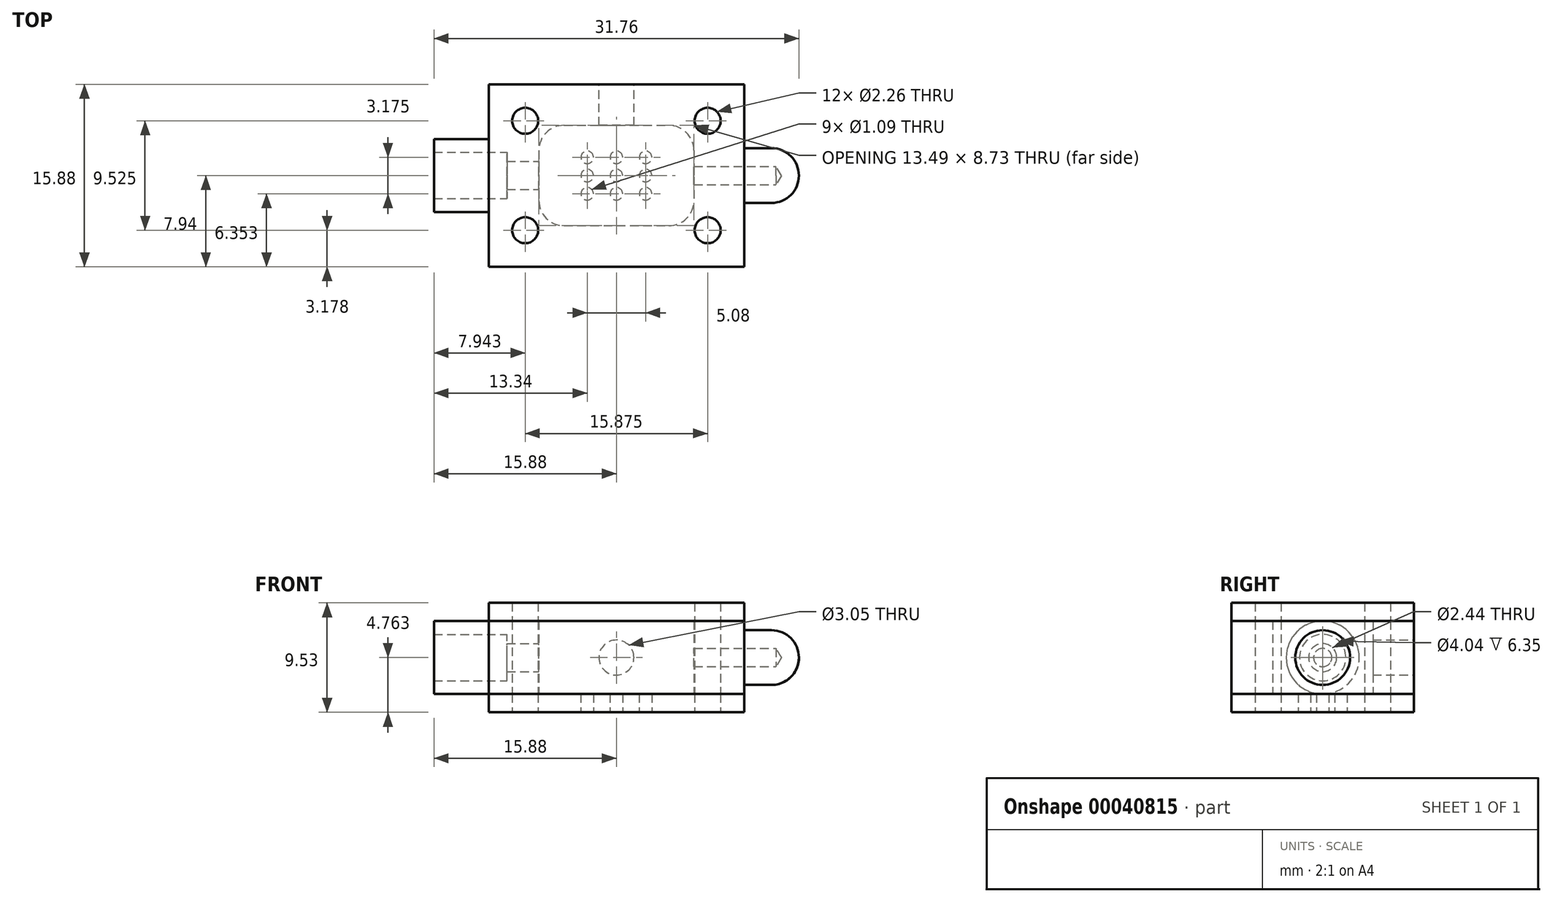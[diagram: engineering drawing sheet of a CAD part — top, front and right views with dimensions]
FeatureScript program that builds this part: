
annotation { "Feature Type Name" : "Feature", "Feature Type Description" : "" }
export const myFeature = defineFeature(function(context is Context, id is Id, definition is map)
    precondition{}
    {
        {
            var Q0;
            Q0=qCreatedBy(makeId("Top.planeOp"),FACE);
            var sketch = newSketch(context, id + "F0", { "sketchPlane" : qUnion([Q0])});
            skLineSegment(sketch, "E0.rect.bottom", {"start": v(-11.11, 7.94) * mm, "end": v(11.11, 7.94) * mm});
            skLineSegment(sketch, "E0.rect.top", {"start": v(-11.11, -7.94) * mm, "end": v(11.11, -7.94) * mm});
            skLineSegment(sketch, "E0.rect.left", {"start": v(-11.11, 7.94) * mm, "end": v(-11.11, -7.94) * mm});
            skLineSegment(sketch, "E0.rect.right", {"start": v(11.11, 7.94) * mm, "end": v(11.11, -7.94) * mm});
            skPoint(sketch, "E0.rect.middle", {"position": v(0, 0) * mm});
            skLineSegment(sketch, "E1.rect.bottom", {"start": v(-4.56, 4.37) * mm, "end": v(4.56, 4.37) * mm});
            skLineSegment(sketch, "E1.rect.top", {"start": v(-4.56, -4.37) * mm, "end": v(4.56, -4.37) * mm});
            skLineSegment(sketch, "E1.rect.left", {"start": v(-6.75, 2.18) * mm, "end": v(-6.75, -2.18) * mm});
            skLineSegment(sketch, "E1.rect.right", {"start": v(6.75, 2.18) * mm, "end": v(6.75, -2.18) * mm});
            skPoint(sketch, "E2.visualSharp", {"position": v(-6.75, 4.37) * mm});
            skArc(sketch, "E2.filletArc", {"start": v(-4.56, 4.37) * mm, "mid": v(-6.1, 3.73) * mm, "end": v(-6.75, 2.18) * mm});
            skPoint(sketch, "E3.visualSharp", {"position": v(-6.75, -4.37) * mm});
            skArc(sketch, "E3.filletArc", {"start": v(-6.75, -2.18) * mm, "mid": v(-6.1, -3.73) * mm, "end": v(-4.56, -4.37) * mm});
            skPoint(sketch, "E4.visualSharp", {"position": v(6.75, -4.37) * mm});
            skArc(sketch, "E4.filletArc", {"start": v(4.56, -4.37) * mm, "mid": v(6.1, -3.73) * mm, "end": v(6.75, -2.18) * mm});
            skPoint(sketch, "E5.visualSharp", {"position": v(6.75, 4.37) * mm});
            skArc(sketch, "E5.filletArc", {"start": v(6.75, 2.18) * mm, "mid": v(6.1, 3.73) * mm, "end": v(4.56, 4.37) * mm});
            skSolve(sketch);
        }
        {
            var Q0;
            Q0=makeQuery(id+"F0.imprint","IMPRINT",FACE,{"disambiguationData":[TD([[makeQuery(id+"F0.imprint","IMPRINT",EDGE,{"derivedFrom":sQuery(id+"F0.wireOp",EDGE,"E0.rect.bottom")}),-1.0]])]});
            extrude(context, id + "F1", {"entities" : qUnion([Q0]), "depth" : 6.35 * mm});
        }
        {
            var Q0;
            Q0=makeQuery(id+"F1.opExtrude","CAP_FACE",FACE,{"disambiguationData":[OSD([sQuery(id+"F0.wireOp",EDGE,"E0.rect.bottom"),sQuery(id+"F0.wireOp",EDGE,"E0.rect.top"),sQuery(id+"F0.wireOp",EDGE,"E0.rect.left"),sQuery(id+"F0.wireOp",EDGE,"E0.rect.right"),sQuery(id+"F0.wireOp",EDGE,"E1.rect.bottom"),sQuery(id+"F0.wireOp",EDGE,"E1.rect.top"),sQuery(id+"F0.wireOp",EDGE,"E1.rect.left"),sQuery(id+"F0.wireOp",EDGE,"E1.rect.right"),sQuery(id+"F0.wireOp",EDGE,"E2.filletArc"),sQuery(id+"F0.wireOp",EDGE,"E3.filletArc"),sQuery(id+"F0.wireOp",EDGE,"E4.filletArc"),sQuery(id+"F0.wireOp",EDGE,"E5.filletArc")])],"isStart":false});
            var sketch = newSketch(context, id + "F2", { "sketchPlane" : qUnion([Q0])});
            skLineSegment(sketch, "E6", {"start": v(-7.94, 10.98) * mm, "end": v(-7.94, -12.77) * mm, "construction": true});
            skLineSegment(sketch, "E7", {"start": v(7.94, 10.98) * mm, "end": v(7.94, -12.77) * mm, "construction": true});
            skLineSegment(sketch, "E8", {"start": v(13.6, 4.76) * mm, "end": v(-15.56, 4.76) * mm, "construction": true});
            skLineSegment(sketch, "E9", {"start": v(13.6, -4.76) * mm, "end": v(-15.56, -4.76) * mm, "construction": true});
            skPoint(sketch, "E10", {"position": v(-7.94, 4.76) * mm});
            skPoint(sketch, "E11", {"position": v(7.94, 4.76) * mm});
            skPoint(sketch, "E12", {"position": v(7.94, -4.76) * mm});
            skPoint(sketch, "E13", {"position": v(-7.94, -4.76) * mm});
            skSolve(sketch);
        }
        {
            var Q0;
            Q0=sQuery(id+"F2.wireOp",VERTEX,"E10");
            var Q1;
            Q1=sQuery(id+"F2.wireOp",VERTEX,"E11");
            var Q2;
            Q2=sQuery(id+"F2.wireOp",VERTEX,"E12");
            var Q3;
            Q3=sQuery(id+"F2.wireOp",VERTEX,"E13");
            var Q4;
            Q4=makeQuery(id+"F1.opExtrude","SWEPT_BODY",BODY,{"disambiguationData":[OSD([sQuery(id+"F0.wireOp",EDGE,"E0.rect.bottom"),sQuery(id+"F0.wireOp",EDGE,"E0.rect.top"),sQuery(id+"F0.wireOp",EDGE,"E0.rect.left"),sQuery(id+"F0.wireOp",EDGE,"E0.rect.right"),sQuery(id+"F0.wireOp",EDGE,"E1.rect.bottom"),sQuery(id+"F0.wireOp",EDGE,"E1.rect.top"),sQuery(id+"F0.wireOp",EDGE,"E1.rect.left"),sQuery(id+"F0.wireOp",EDGE,"E1.rect.right"),sQuery(id+"F0.wireOp",EDGE,"E2.filletArc"),sQuery(id+"F0.wireOp",EDGE,"E3.filletArc"),sQuery(id+"F0.wireOp",EDGE,"E4.filletArc"),sQuery(id+"F0.wireOp",EDGE,"E5.filletArc")])]});
            hole(context, id + "F3", {"style" : HoleStyle.SIMPLE, "holeDiameter" : 2.26 * mm, "endStyle" : HoleEndStyle.THROUGH, "locations" : qUnion([Q0, Q1, Q2, Q3]), "scope" : qUnion([Q4])});
        }
        {
            var Q0;
            Q0=makeQuery(id+"F1.opExtrude","SWEPT_FACE",FACE,{"disambiguationData":[OSD([sQuery(id+"F0.wireOp",EDGE,"E0.rect.left")])]});
            var sketch = newSketch(context, id + "F4", { "sketchPlane" : qUnion([Q0])});
            skCircle(sketch, "E14", {"center": v(0, 3.18) * mm, "radius": 3.18 * mm});
            skSolve(sketch);
        }
        {
            var Q0;
            Q0 = qSketchRegion(id + "F4", true);
            extrude(context, id + "F5", {"entities" : qUnion([Q0]), "operationType" : NewBodyOperationType.ADD, "depth" : 4.76 * mm});
        }
        {
            var Q0;
            Q0=makeQuery(id+"F5.opExtrude","CAP_FACE",FACE,{"disambiguationData":[OSD([sQuery(id+"F4.wireOp",EDGE,"E14")])],"isStart":false});
            var sketch = newSketch(context, id + "F6", { "sketchPlane" : qUnion([Q0])});
            skPoint(sketch, "E15", {"position": v(0, 3.18) * mm});
            skSolve(sketch);
        }
        {
            var Q0;
            Q0=makeQuery(id+"F1.opExtrude","SWEPT_FACE",FACE,{"disambiguationData":[OSD([sQuery(id+"F0.wireOp",EDGE,"E0.rect.right")])]});
            var sketch = newSketch(context, id + "F7", { "sketchPlane" : qUnion([Q0])});
            skCircle(sketch, "E16", {"center": v(0, 3.18) * mm, "radius": 2.38 * mm});
            skPoint(sketch, "E16.centerSnap0", {"position": v(0, 6.35) * mm});
            skSolve(sketch);
        }
        {
            var Q0;
            Q0 = qSketchRegion(id + "F7", true);
            extrude(context, id + "F8", {"entities" : qUnion([Q0]), "operationType" : NewBodyOperationType.ADD, "depth" : 4.76 * mm});
        }
        {
            var Q0;
            Q0=makeQuery(id+"F8.opExtrude","CAP_EDGE",EDGE,{"disambiguationData":[OSD([sQuery(id+"F7.wireOp",EDGE,"E16")])],"isStart":false});
            fillet(context, id + "F9", {"entities" : qUnion([Q0]), "radius" : 2.38 * mm, "tangentPropagation" : true, "allowEdgeOverflow" : false});
        }
        {
            var Q0;
            Q0=makeQuery(id+"F1.opExtrude","SWEPT_FACE",FACE,{"disambiguationData":[OSD([sQuery(id+"F0.wireOp",EDGE,"E1.rect.right")])]});
            var sketch = newSketch(context, id + "F10", { "sketchPlane" : qUnion([Q0])});
            skPoint(sketch, "E17", {"position": v(0, 3.18) * mm});
            skSolve(sketch);
        }
        {
            var Q0;
            Q0=makeQuery(id+"F5.opExtrude","CAP_FACE",FACE,{"disambiguationData":[OSD([sQuery(id+"F4.wireOp",EDGE,"E14")])],"isStart":false});
            cPlane(context, id + "F11", {"entities" : qUnion([Q0]), "cplaneType" : CPlaneType.OFFSET, "offset" : 0 * mm, "width" : 152.4 * mm, "height" : 152.4 * mm});
        }
        {
            var Q0;
            Q0=sQuery(id+"F10.wireOp",VERTEX,"E17");
            var Q1;
            Q1=makeQuery(id+"F1.opExtrude","SWEPT_BODY",BODY,{"disambiguationData":[OSD([sQuery(id+"F0.wireOp",EDGE,"E0.rect.bottom"),sQuery(id+"F0.wireOp",EDGE,"E0.rect.top"),sQuery(id+"F0.wireOp",EDGE,"E0.rect.left"),sQuery(id+"F0.wireOp",EDGE,"E0.rect.right"),sQuery(id+"F0.wireOp",EDGE,"E1.rect.bottom"),sQuery(id+"F0.wireOp",EDGE,"E1.rect.top"),sQuery(id+"F0.wireOp",EDGE,"E1.rect.left"),sQuery(id+"F0.wireOp",EDGE,"E1.rect.right"),sQuery(id+"F0.wireOp",EDGE,"E2.filletArc"),sQuery(id+"F0.wireOp",EDGE,"E3.filletArc"),sQuery(id+"F0.wireOp",EDGE,"E4.filletArc"),sQuery(id+"F0.wireOp",EDGE,"E5.filletArc")])]});
            hole(context, id + "F12", {"style" : HoleStyle.SIMPLE, "holeDiameter" : 1.59 * mm, "endStyle" : HoleEndStyle.BLIND, "holeDepth" : 7.14 * mm, "locations" : qUnion([Q0]), "scope" : qUnion([Q1])});
        }
        {
            var Q0;
            Q0=qCreatedBy(id+"F11.planeOp",FACE);
            var sketch = newSketch(context, id + "F13", { "sketchPlane" : qUnion([Q0])});
            skPoint(sketch, "E18", {"position": v(0, 3.18) * mm});
            skSolve(sketch);
        }
        {
            var Q0;
            Q0=sQuery(id+"F13.wireOp",VERTEX,"E18");
            var Q1;
            Q1=makeQuery(id+"F1.opExtrude","SWEPT_BODY",BODY,{"disambiguationData":[OSD([sQuery(id+"F0.wireOp",EDGE,"E0.rect.bottom"),sQuery(id+"F0.wireOp",EDGE,"E0.rect.top"),sQuery(id+"F0.wireOp",EDGE,"E0.rect.left"),sQuery(id+"F0.wireOp",EDGE,"E0.rect.right"),sQuery(id+"F0.wireOp",EDGE,"E1.rect.bottom"),sQuery(id+"F0.wireOp",EDGE,"E1.rect.top"),sQuery(id+"F0.wireOp",EDGE,"E1.rect.left"),sQuery(id+"F0.wireOp",EDGE,"E1.rect.right"),sQuery(id+"F0.wireOp",EDGE,"E2.filletArc"),sQuery(id+"F0.wireOp",EDGE,"E3.filletArc"),sQuery(id+"F0.wireOp",EDGE,"E4.filletArc"),sQuery(id+"F0.wireOp",EDGE,"E5.filletArc")])]});
            hole(context, id + "F14", {"style" : HoleStyle.C_BORE, "holeDiameter" : 2.44 * mm, "cBoreDiameter" : 4.04 * mm, "cBoreDepth" : 6.35 * mm, "endStyle" : HoleEndStyle.BLIND, "holeDepth" : 11.1 * mm, "locations" : qUnion([Q0]), "scope" : qUnion([Q1])});
        }
        {
            var Q0;
            Q0=makeQuery(id+"F1.opExtrude","SWEPT_FACE",FACE,{"disambiguationData":[OSD([sQuery(id+"F0.wireOp",EDGE,"E0.rect.bottom")])]});
            var sketch = newSketch(context, id + "F15", { "sketchPlane" : qUnion([Q0])});
            skCircle(sketch, "E19", {"center": v(0, 3.18) * mm, "radius": 1.52 * mm});
            skSolve(sketch);
        }
        {
            var Q0;
            Q0 = qSketchRegion(id + "F15", true);
            var Q1;
            Q1=makeQuery(id+"F1.opExtrude","SWEPT_FACE",FACE,{"disambiguationData":[OSD([sQuery(id+"F0.wireOp",EDGE,"E1.rect.bottom")])]});
            extrude(context, id + "F16", {"entities" : qUnion([Q0]), "operationType" : NewBodyOperationType.REMOVE, "endBound" : BoundingType.UP_TO_SURFACE, "oppositeDirection" : true, "endBoundEntityFace" : qUnion([Q1]), "depth" : 25.4 * mm});
        }
        {
            var Q0;
            Q0=makeQuery(id+"F1.opExtrude","SWEPT_BODY",BODY,{"disambiguationData":[OSD([sQuery(id+"F0.wireOp",EDGE,"E0.rect.bottom"),sQuery(id+"F0.wireOp",EDGE,"E0.rect.top"),sQuery(id+"F0.wireOp",EDGE,"E0.rect.left"),sQuery(id+"F0.wireOp",EDGE,"E0.rect.right"),sQuery(id+"F0.wireOp",EDGE,"E1.rect.bottom"),sQuery(id+"F0.wireOp",EDGE,"E1.rect.top"),sQuery(id+"F0.wireOp",EDGE,"E1.rect.left"),sQuery(id+"F0.wireOp",EDGE,"E1.rect.right"),sQuery(id+"F0.wireOp",EDGE,"E2.filletArc"),sQuery(id+"F0.wireOp",EDGE,"E3.filletArc"),sQuery(id+"F0.wireOp",EDGE,"E4.filletArc"),sQuery(id+"F0.wireOp",EDGE,"E5.filletArc")])]});
            transform(context, id + "F17", {"entities" : qUnion([Q0]), "transformType" : TransformType.TRANSLATION_3D, "dx" : 0 * mm, "dy" : 0 * mm, "dz" : 1.59 * mm, "makeCopy" : false});
        }
        {
            var Q0;
            Q0=qCreatedBy(makeId("Top.planeOp"),FACE);
            var sketch = newSketch(context, id + "F18", { "sketchPlane" : qUnion([Q0])});
            skLineSegment(sketch, "E20.rect.bottom", {"start": v(-11.11, 7.94) * mm, "end": v(11.11, 7.94) * mm});
            skLineSegment(sketch, "E20.rect.top", {"start": v(-11.11, -7.94) * mm, "end": v(11.11, -7.94) * mm});
            skLineSegment(sketch, "E20.rect.left", {"start": v(-11.11, 7.94) * mm, "end": v(-11.11, -7.94) * mm});
            skLineSegment(sketch, "E20.rect.right", {"start": v(11.11, 7.94) * mm, "end": v(11.11, -7.94) * mm});
            skPoint(sketch, "E20.rect.middle", {"position": v(0, 0) * mm});
            skLineSegment(sketch, "E21", {"start": v(-18.07, 4.76) * mm, "end": v(17.58, 4.76) * mm, "construction": true});
            skLineSegment(sketch, "E22", {"start": v(-17.42, -4.76) * mm, "end": v(16.77, -4.76) * mm, "construction": true});
            skLineSegment(sketch, "E23", {"start": v(7.94, 12.45) * mm, "end": v(7.94, -13.92) * mm, "construction": true});
            skLineSegment(sketch, "E24", {"start": v(-7.94, 11.31) * mm, "end": v(-7.94, -14.4) * mm, "construction": true});
            skCircle(sketch, "E25", {"center": v(-7.94, 4.76) * mm, "radius": 1.13 * mm});
            skCircle(sketch, "E26", {"center": v(7.94, 4.76) * mm, "radius": 1.13 * mm});
            skCircle(sketch, "E27", {"center": v(7.94, -4.76) * mm, "radius": 1.13 * mm});
            skCircle(sketch, "E28", {"center": v(-7.94, -4.76) * mm, "radius": 1.13 * mm});
            skLineSegment(sketch, "E29", {"start": v(-2.54, 3.14) * mm, "end": v(-2.54, -3.4) * mm, "construction": true});
            skLineSegment(sketch, "E30", {"start": v(2.54, 3) * mm, "end": v(2.54, -2.94) * mm, "construction": true});
            skLineSegment(sketch, "E31", {"start": v(-3.46, 1.59) * mm, "end": v(3.77, 1.59) * mm, "construction": true});
            skLineSegment(sketch, "E32", {"start": v(-3.4, -1.59) * mm, "end": v(3.14, -1.59) * mm, "construction": true});
            skCircle(sketch, "E33", {"center": v(-2.54, 1.59) * mm, "radius": 0.55 * mm});
            skCircle(sketch, "E34", {"center": v(-2.54, 0) * mm, "radius": 0.55 * mm});
            skCircle(sketch, "E35", {"center": v(-2.54, -1.59) * mm, "radius": 0.55 * mm});
            skCircle(sketch, "E36", {"center": v(0, -1.59) * mm, "radius": 0.55 * mm});
            skCircle(sketch, "E37", {"center": v(0, 0) * mm, "radius": 0.55 * mm});
            skCircle(sketch, "E38", {"center": v(0, 1.59) * mm, "radius": 0.55 * mm});
            skCircle(sketch, "E39", {"center": v(2.54, 1.59) * mm, "radius": 0.55 * mm});
            skCircle(sketch, "E40", {"center": v(2.54, 0) * mm, "radius": 0.55 * mm});
            skPoint(sketch, "E40.centerSnap0", {"position": v(2.54, 0.03) * mm});
            skCircle(sketch, "E41", {"center": v(2.54, -1.59) * mm, "radius": 0.55 * mm});
            skSolve(sketch);
        }
        {
            var Q0;
            Q0=makeQuery(id+"F18.imprint","IMPRINT",FACE,{"disambiguationData":[TD([[makeQuery(id+"F18.imprint","IMPRINT",EDGE,{"derivedFrom":sQuery(id+"F18.wireOp",EDGE,"E20.rect.bottom")}),-1.0]])]});
            extrude(context, id + "F19", {"entities" : qUnion([Q0]), "depth" : 1.59 * mm});
        }
        {
            var Q0;
            Q0=makeQuery(id+"F1.opExtrude","CAP_FACE",FACE,{"disambiguationData":[OSD([sQuery(id+"F0.wireOp",EDGE,"E0.rect.bottom"),sQuery(id+"F0.wireOp",EDGE,"E0.rect.top"),sQuery(id+"F0.wireOp",EDGE,"E0.rect.left"),sQuery(id+"F0.wireOp",EDGE,"E0.rect.right"),sQuery(id+"F0.wireOp",EDGE,"E1.rect.bottom"),sQuery(id+"F0.wireOp",EDGE,"E1.rect.top"),sQuery(id+"F0.wireOp",EDGE,"E1.rect.left"),sQuery(id+"F0.wireOp",EDGE,"E1.rect.right"),sQuery(id+"F0.wireOp",EDGE,"E2.filletArc"),sQuery(id+"F0.wireOp",EDGE,"E3.filletArc"),sQuery(id+"F0.wireOp",EDGE,"E4.filletArc"),sQuery(id+"F0.wireOp",EDGE,"E5.filletArc")])],"isStart":false});
            cPlane(context, id + "F20", {"entities" : qUnion([Q0]), "cplaneType" : CPlaneType.OFFSET, "offset" : 0 * mm, "width" : 152.4 * mm, "height" : 152.4 * mm});
        }
        {
            var Q0;
            Q0=qCreatedBy(id+"F20.planeOp",FACE);
            var sketch = newSketch(context, id + "F21", { "sketchPlane" : qUnion([Q0])});
            skLineSegment(sketch, "E42.rect.bottom", {"start": v(-11.11, 7.94) * mm, "end": v(11.11, 7.94) * mm});
            skLineSegment(sketch, "E42.rect.top", {"start": v(-11.11, -7.94) * mm, "end": v(11.11, -7.94) * mm});
            skLineSegment(sketch, "E42.rect.left", {"start": v(-11.11, 7.94) * mm, "end": v(-11.11, -7.94) * mm});
            skLineSegment(sketch, "E42.rect.right", {"start": v(11.11, 7.94) * mm, "end": v(11.11, -7.94) * mm});
            skPoint(sketch, "E42.rect.middle", {"position": v(0, 0) * mm});
            skLineSegment(sketch, "E43", {"start": v(-14.16, 4.76) * mm, "end": v(14.81, 4.76) * mm, "construction": true});
            skLineSegment(sketch, "E44", {"start": v(-14.33, -4.76) * mm, "end": v(15.3, -4.76) * mm, "construction": true});
            skLineSegment(sketch, "E45", {"start": v(-7.94, 12.45) * mm, "end": v(-7.94, -13.43) * mm, "construction": true});
            skLineSegment(sketch, "E46", {"start": v(7.94, 11.8) * mm, "end": v(7.94, -13.92) * mm, "construction": true});
            skCircle(sketch, "E47", {"center": v(-7.94, 4.76) * mm, "radius": 1.13 * mm});
            skCircle(sketch, "E48", {"center": v(7.94, 4.76) * mm, "radius": 1.13 * mm});
            skCircle(sketch, "E49", {"center": v(7.94, -4.76) * mm, "radius": 1.13 * mm});
            skCircle(sketch, "E50", {"center": v(-7.94, -4.76) * mm, "radius": 1.13 * mm});
            skSolve(sketch);
        }
        {
            var Q0;
            Q0 = qSketchRegion(id + "F21", true);
            extrude(context, id + "F22", {"entities" : qUnion([Q0]), "depth" : 1.59 * mm});
        }
    });
